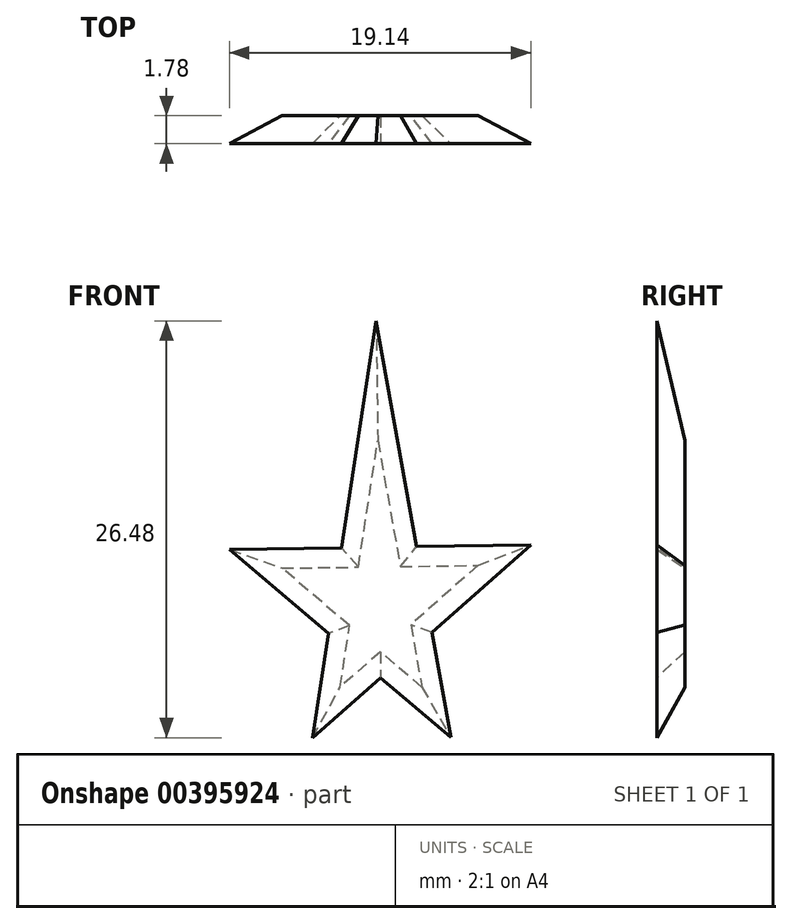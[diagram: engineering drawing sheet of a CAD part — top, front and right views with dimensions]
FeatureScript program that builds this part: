
annotation { "Feature Type Name" : "Feature", "Feature Type Description" : "" }
export const myFeature = defineFeature(function(context is Context, id is Id, definition is map)
    precondition{}
    {
        {
            var Q0;
            Q0=qCreatedBy(makeId("Front.planeOp"),FACE);
            var sketch = newSketch(context, id + "F0", { "sketchPlane" : qUnion([Q0])});
            skLineSegment(sketch, "E0", {"start": v(2.76, -15.92) * mm, "end": v(-0.05, -0.25) * mm});
            skLineSegment(sketch, "E1", {"start": v(-0.05, -0.25) * mm, "end": v(-2.44, -15.92) * mm});
            skLineSegment(sketch, "E2", {"start": v(-2.44, -15.92) * mm, "end": v(6.32, -8.18) * mm});
            skLineSegment(sketch, "E3", {"start": v(2.76, -15.92) * mm, "end": v(-6.14, -8.36) * mm});
            skLineSegment(sketch, "E4", {"start": v(-6.14, -8.36) * mm, "end": v(6.32, -8.18) * mm});
            skSolve(sketch);
        }
        {
            var Q0;
            {var subQ0=sQuery(id+"F0.wireOp",EDGE,"E4");var subQ1=sQuery(id+"F0.wireOp",EDGE,"E1");var subQ2=makeQuery(id+"F0.imprint","INTERSECT",VERTEX,{"derivedFrom":[subQ1,subQ0]});Q0=makeQuery(id+"F0.imprint","IMPRINT",FACE,{"disambiguationData":[TD([[makeQuery(id+"F0.imprint","IMPRINT",EDGE,{"disambiguationData":[TD([[subQ2,-1.0]])],"derivedFrom":subQ1}),-1.0]])]});}
            var Q1;
            {var subQ3=sQuery(id+"F0.wireOp",EDGE,"E2");var subQ5=sQuery(id+"F0.wireOp",EDGE,"E0");var subQ6=makeQuery(id+"F0.imprint","INTERSECT",VERTEX,{"derivedFrom":[subQ5,subQ3]});Q1=makeQuery(id+"F0.imprint","IMPRINT",FACE,{"disambiguationData":[TD([[makeQuery(id+"F0.imprint","IMPRINT",EDGE,{"disambiguationData":[TD([[subQ6,-1.0]])],"derivedFrom":subQ5}),1.0]])]});}
            var Q2;
            {var subQ0=sQuery(id+"F0.wireOp",EDGE,"E2");var subQ1=sQuery(id+"F0.wireOp",EDGE,"E0");var subQ2=makeQuery(id+"F0.imprint","INTERSECT",VERTEX,{"derivedFrom":[subQ1,subQ0]});Q2=makeQuery(id+"F0.imprint","IMPRINT",FACE,{"disambiguationData":[TD([[makeQuery(id+"F0.imprint","IMPRINT",EDGE,{"disambiguationData":[TD([[subQ2,-1.0]])],"derivedFrom":subQ1}),-1.0]])]});}
            var Q3;
            {var subQ0=sQuery(id+"F0.wireOp",EDGE,"E1");var subQ1=sQuery(id+"F0.wireOp",EDGE,"E0");var subQ2=makeQuery(id+"F0.imprint","INTERSECT",VERTEX,{"derivedFrom":[subQ1,subQ0]});Q3=makeQuery(id+"F0.imprint","IMPRINT",FACE,{"disambiguationData":[TD([[makeQuery(id+"F0.imprint","IMPRINT",EDGE,{"disambiguationData":[TD([[subQ2,1.0]])],"derivedFrom":subQ1}),1.0]])]});}
            var Q4;
            {var subQ0=sQuery(id+"F0.wireOp",EDGE,"E3");var subQ1=sQuery(id+"F0.wireOp",EDGE,"E0");var subQ2=makeQuery(id+"F0.imprint","INTERSECT",VERTEX,{"derivedFrom":[subQ1,subQ0]});Q4=makeQuery(id+"F0.imprint","IMPRINT",FACE,{"disambiguationData":[TD([[makeQuery(id+"F0.imprint","IMPRINT",EDGE,{"disambiguationData":[TD([[subQ2,-1.0]])],"derivedFrom":subQ1}),1.0]])]});}
            var Q5;
            {var subQ0=sQuery(id+"F0.wireOp",EDGE,"E2");var subQ1=sQuery(id+"F0.wireOp",EDGE,"E1");var subQ2=makeQuery(id+"F0.imprint","INTERSECT",VERTEX,{"derivedFrom":[subQ1,subQ0]});Q5=makeQuery(id+"F0.imprint","IMPRINT",FACE,{"disambiguationData":[TD([[makeQuery(id+"F0.imprint","IMPRINT",EDGE,{"disambiguationData":[TD([[subQ2,1.0]])],"derivedFrom":subQ1}),1.0]])]});}
            extrude(context, id + "F1", {"entities" : qUnion([Q0, Q1, Q2, Q3, Q4, Q5]), "depth" : 1.78 * mm, "hasDraft" : true, "draftAngle" : 35 * degree});
        }
    });
